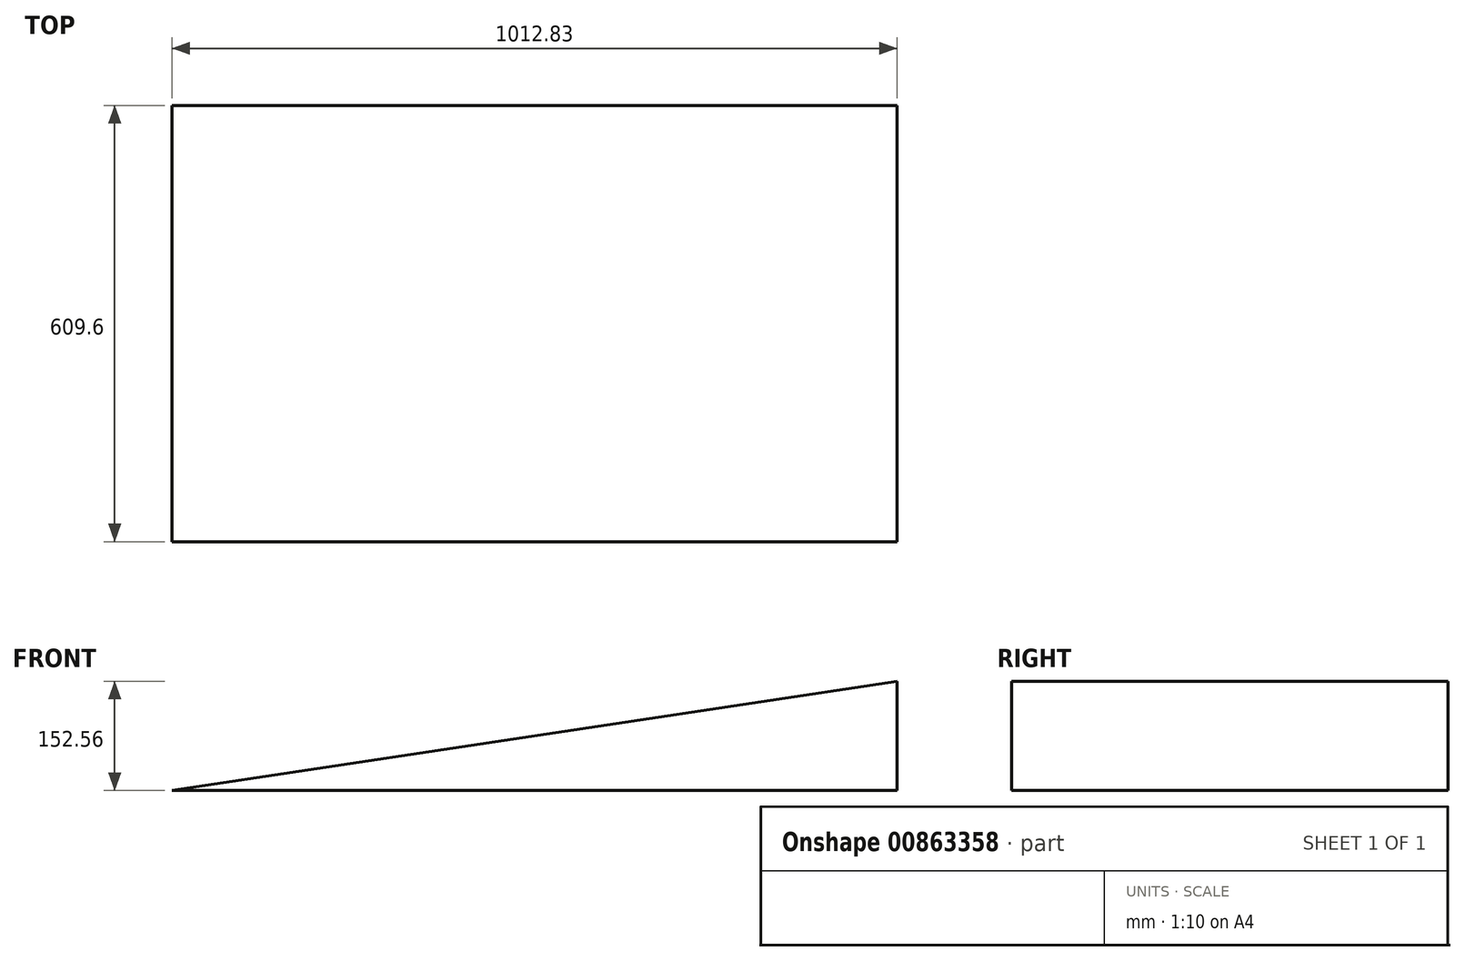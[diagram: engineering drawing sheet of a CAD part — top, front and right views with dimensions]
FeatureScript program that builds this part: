
annotation { "Feature Type Name" : "Feature", "Feature Type Description" : "" }
export const myFeature = defineFeature(function(context is Context, id is Id, definition is map)
    precondition{}
    {
        {
            var Q0;
            Q0=qCreatedBy(makeId("Front.planeOp"),FACE);
            var sketch = newSketch(context, id + "F0", { "sketchPlane" : qUnion([Q0])});
            skLineSegment(sketch, "E0", {"start": v(0, 0) * mm, "end": v(758.83, 0) * mm});
            skLineSegment(sketch, "E1", {"start": v(758.83, 0) * mm, "end": v(758.83, 114.3) * mm});
            skLineSegment(sketch, "E2", {"start": v(758.83, 0) * mm, "end": v(1012.83, 0) * mm});
            skLineSegment(sketch, "E3", {"start": v(1012.83, 0) * mm, "end": v(1012.83, 152.56) * mm});
            skLineSegment(sketch, "E4", {"start": v(0, 0) * mm, "end": v(758.83, 114.3) * mm});
            skLineSegment(sketch, "E5", {"start": v(758.83, 114.3) * mm, "end": v(1012.83, 152.56) * mm});
            skSolve(sketch);
        }
        {
            var Q0;
            Q0 = qSketchRegion(id + "F0", true);
            extrude(context, id + "F1", {"entities" : qUnion([Q0]), "depth" : 609.6 * mm, "offsetDistance" : 25.4 * mm});
        }
    });
